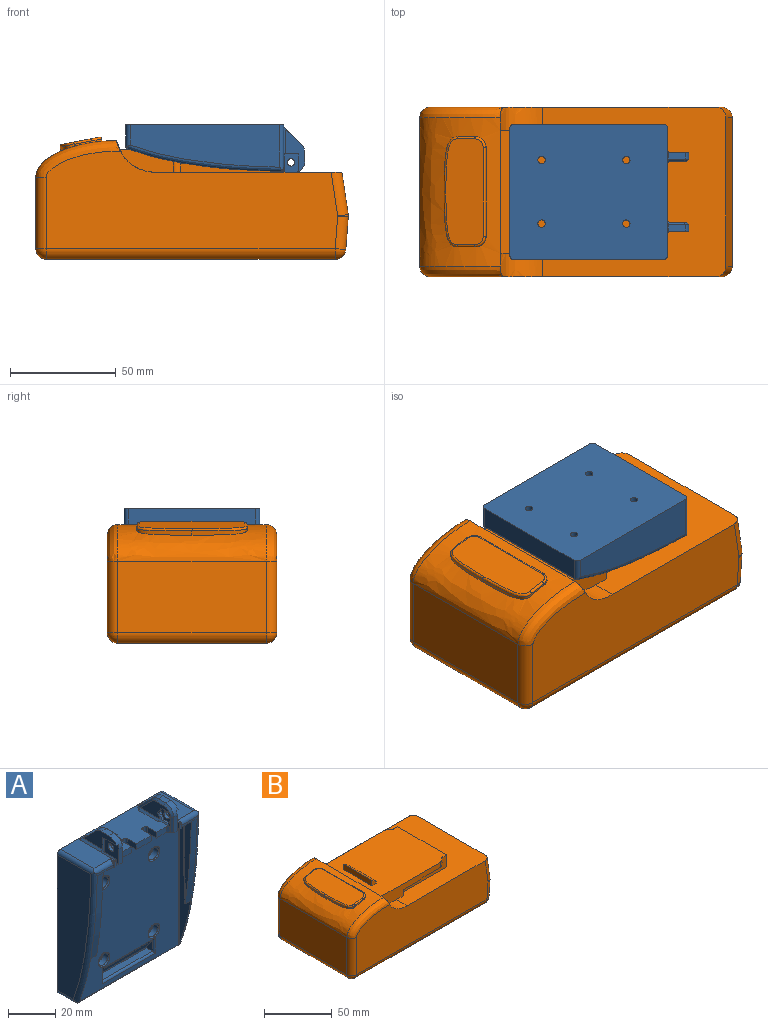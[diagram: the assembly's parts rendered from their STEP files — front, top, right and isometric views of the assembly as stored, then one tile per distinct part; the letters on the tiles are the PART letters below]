
ASSEMBLY  parts=2 mates=1
PART A: 203 faces, bbox 64.2x22.7x84.8 mm
  f0: sphere r=1mm, area 0.3mm2, adj f3,f4,f9,f104
  f1: plane 3.46x1mm, normal (0,0,-1), area 3.5mm2, adj f7,f12,f16,f17
  f2: plane 3x2.62mm, normal (0,0.95,-0.32), area 8.1mm2, adj f4,f21,f105,f106,f107
  f3: cylinder r=1mm len=2.5mm, axis (1,0,0), area 0.8mm2, adj f0,f4,f10,f21
  f4: plane 13.43x3.2mm, normal (0,1,0), area 39.7mm2, adj f0,f2,f3,f21,f104
  f5: plane 25.37x2.5mm, normal (0,1,0), area 63.4mm2, adj f6,f8,f21,f22,f107
  f6: cylinder r=0.5mm len=5.3mm, axis (0,1,0), area 4.2mm2, adj f5,f21,f22,f23
  f7: plane 3x1.73mm, normal (0,-0.87,-0.5), area 3.5mm2, adj f1,f12,f28,f29
  f8: cylinder r=1mm len=27.87mm, axis (0,0,-1), area 41.8mm2, adj f5,f24,f32,f106
  f9: cylinder r=1mm len=1mm, axis (0,-1,0), area 0.2mm2, adj f0,f10,f32,f33,f104
  f10: plane 2.5x0.06mm, normal (0,0,-1), area 0.1mm2, adj f3,f9,f21,f33
  f11: cylinder r=5mm len=3.54mm, axis (1,0,0), area 11.8mm2, adj f13,f15,f31,f37
  f12: plane 6.93x6mm, normal (1,0,0), area 21.6mm2, adj f1,f7,f17,f18,f27,f28,f38
  f13: plane 4.43x3mm, normal (0,0,1), area 13.3mm2, adj f11,f14,f37,f40
  f14: plane 4.43x1mm, normal (0.71,0,0.71), area 6.3mm2, adj f13,f15,f41,f42
  f15: cone r=4mm half-angle=45deg, axis (-1,0,0), area 5mm2, adj f11,f14,f30,f42
  f16: plane 4.04x0.5mm, normal (0.71,0,-0.71), area 2.7mm2, adj f1,f29,f42,f43
  f17: plane 3x1.73mm, normal (0,0.87,-0.5), area 3.5mm2, adj f1,f12,f18,f43
  f18: plane 3x1.73mm, normal (0,0.87,0.5), area 3.5mm2, adj f12,f17,f27,f44
  f19: plane 6x6mm, normal (0,-1,0), area 12.4mm2, adj f26,f47
  f20: plane 6x6mm, normal (0,-1,0), area 12.4mm2, adj f25,f48
  f21: plane 66.43x7.22mm, normal (1,0,0), area 322.6mm2, adj f2,f3,f4,f5,f6,f10,f45,f50
  f22: plane 5.3x2mm, normal (0,0,-1), area 10.6mm2, adj f5,f6,f24,f51
  f23: sphere r=0.5mm, area 0.5mm2, adj f6,f50,f51
  f24: cylinder r=1mm len=6.3mm, axis (0,-1,0), area 9.1mm2, adj f8,f22,f32,f52
  f25: cylinder r=3mm len=6mm, axis (0,-1,0), area 56.5mm2, adj f20,f54
  f26: cylinder r=3mm len=6mm, axis (0,-1,0), area 56.5mm2, adj f19,f55
  f27: plane 3.46x1mm, normal (0,0,1), area 3.5mm2, adj f12,f18,f28,f56
  f28: plane 3x1.73mm, normal (0,-0.87,0.5), area 3.5mm2, adj f7,f12,f27,f57
  f29: plane 3.5x2.31mm, normal (0.71,-0.61,-0.35), area 2.7mm2, adj f7,f16,f42,f57
  f30: plane 8.95x8.24mm, normal (0.71,0.5,0.5), area 15.1mm2, adj f15,f31,f42,f59
  f31: plane 8.24x8.24mm, normal (0,0.71,0.71), area 35.3mm2, adj f11,f30,f37,f60,f61
  f32: plane 44.58x10.5mm, normal (1,0,0), area 131.8mm2, adj f8,f9,f24,f33,f53,f65,f104,f105
  f33: extruded ~45x4mm, area 157.9mm2, adj f9,f10,f32,f45,f65,f66
  f34: plane 1.5x0.68mm, normal (-1,0,0), area 0.3mm2, adj f63,f64,f67
  f35: sphere r=0.5mm, area 0.4mm2, adj f62,f63,f67
  f36: cylinder r=0.5mm len=1mm, axis (-0.71,0,-0.71), area 0.4mm2, adj f61,f62,f68,f69
  f37: plane 19.99x9mm, normal (-1,0,0), area 84.5mm2, adj f11,f13,f31,f39,f40,f61,f70
  f38: cylinder r=1.75mm len=3.5mm, axis (-1,0,0), area 16.5mm2, adj f12,f71
  f39: plane 8.19x1mm, normal (0,0,-1), area 8.2mm2, adj f37,f40,f70,f71
  f40: cylinder r=5mm len=5mm, axis (-1,0,0), area 21.3mm2, adj f13,f37,f39,f41,f71,f72
  f41: cone r=4mm half-angle=45deg, axis (-1,0,0), area 10mm2, adj f14,f40,f42,f73
  f42: plane 18.09x8mm, normal (1,0,0), area 70.1mm2, adj f14,f15,f16,f29,f30,f41,f43,f57
  f43: plane 3.5x2.15mm, normal (0.71,0.61,-0.35), area 2.6mm2, adj f16,f17,f42,f44,f73
  f44: plane 3.5x2.15mm, normal (0.71,0.61,0.35), area 2.6mm2, adj f18,f43,f56,f73,f74
  f45: bspline ~73.6x12.79mm, area 230.3mm2, adj f21,f33,f46,f49,f50,f64,f66,f82
  f46: bspline ~2.41x2mm, area 0.9mm2, adj f45,f49,f84
  f47: torus R=2.25mm, axis (0,-1,0), area 9.5mm2, adj f19,f85
  f48: torus R=2.25mm, axis (0,-1,0), area 9.5mm2, adj f20,f86
  f49: bspline ~0.88x0.76mm, area 0.1mm2, adj f45,f46,f50,f84,f90
  f50: cylinder r=0.5mm len=66.93mm, axis (0,0,-1), area 52.4mm2, adj f21,f23,f45,f49,f90,f102
  f51: cylinder r=0.5mm len=2mm, axis (1,0,0), area 1.6mm2, adj f22,f23,f52,f102
  f52: torus R=1.5mm, axis (0,1,0), area 1.5mm2, adj f24,f51,f53,f102
  f53: cylinder r=0.5mm len=2.07mm, axis (0,0,-1), area 1.6mm2, adj f32,f52,f89,f102
  f54: torus R=3.5mm, axis (0,1,0), area 15.7mm2, adj f25,f102
  f55: torus R=3.5mm, axis (0,1,0), area 15.7mm2, adj f26,f102
  f56: plane 4.04x0.5mm, normal (0.71,0,0.71), area 2.7mm2, adj f27,f44,f57,f100
  f57: plane 3.5x2.31mm, normal (0.71,-0.61,0.35), area 3.5mm2, adj f28,f29,f42,f56,f58,f100
  f58: plane 11.74x1mm, normal (0.71,0,0.71), area 16.2mm2, adj f42,f57,f59,f100
  f59: bspline ~2.83x2mm, area 2.6mm2, adj f30,f58,f60,f100
  f60: plane 4x0.71mm, normal (0,0.38,0.92), area 2.9mm2, adj f31,f59,f61,f100
  f61: plane 21.41x1mm, normal (-0.71,0,0.71), area 23.3mm2, adj f31,f36,f37,f60,f69,f70,f100
  f62: cylinder r=0.5mm len=0.71mm, axis (1,0,0), area 0.5mm2, adj f35,f36,f68,f100
  f63: cylinder r=0.5mm len=2mm, axis (0,1,0), area 1.1mm2, adj f34,f35,f64,f100
  f64: cylinder r=2mm len=11.44mm, axis (-1,0,0), area 32.7mm2, adj f34,f45,f63,f66,f82,f100
  f65: cylinder r=0.5mm len=10.5mm, axis (0,1,0), area 8.2mm2, adj f32,f33,f89,f96
  f66: plane 9.92x1.14mm, normal (0,-1,0), area 9.7mm2, adj f33,f45,f64,f67,f96
  f67: cylinder r=0.5mm len=2.5mm, axis (0,0,1), area 2mm2, adj f34,f35,f66,f68,f96
  f68: plane 2.79x1mm, normal (0,-1,0), area 2.5mm2, adj f36,f62,f67,f69,f96
  f69: plane 8.91x3.71mm, normal (1,0,0), area 30.4mm2, adj f36,f61,f68,f70,f96
  f70: plane 10.2x1.5mm, normal (0,-1,0), area 12.1mm2, adj f37,f39,f61,f69,f71,f96
  f71: plane 10.2x8.7mm, normal (-1,0,0), area 78.8mm2, adj f38,f39,f40,f70,f72,f96
  f72: plane 8x2mm, normal (0,-1,0), area 16mm2, adj f40,f71,f73,f96
  f73: plane 8x1mm, normal (0.71,-0.71,0), area 11.2mm2, adj f41,f42,f43,f44,f72,f74,f96
  f74: plane 6x1.73mm, normal (1,0,0), area 4.1mm2, adj f44,f73,f75,f96,f100
  f75: plane 3x1mm, normal (0.71,-0.71,0), area 4.2mm2, adj f74,f76,f96,f100
  f76: plane 6x3mm, normal (0,-1,0), area 18mm2, adj f75,f77,f96,f100
  f77: plane 5.5x3mm, normal (1,0,0), area 16.5mm2, adj f76,f78,f96,f100
  f78: cylinder r=1mm len=3mm, axis (0,0,-1), area 4.7mm2, adj f77,f79,f96,f100
  f79: plane 3x1mm, normal (0,-1,0), area 3mm2, adj f78,f80,f96,f100
  f80: cylinder r=1mm len=3mm, axis (0,0,-1), area 4.7mm2, adj f79,f81,f96,f100
  f81: plane 5.5x3mm, normal (-1,0,0), area 16.5mm2, adj f80,f96,f100,f101
  f82: cylinder r=2mm len=21.44mm, axis (0,-1,0), area 65.1mm2, adj f45,f64,f83,f98,f100
  f83: plane 70.51x20.02mm, normal (-1,0,0), area 1180.4mm2, adj f45,f82,f84,f98
  f84: cylinder r=2mm len=10.66mm, axis (0,-1,0), area 32.3mm2, adj f46,f49,f83,f98,f99
  f85: cylinder r=1.75mm len=7mm, axis (0,-1,0), area 77mm2, adj f47,f98
  f86: cylinder r=1.75mm len=7mm, axis (0,-1,0), area 77mm2, adj f48,f98
  f87: plane 5.66x3.46mm, normal (1,0,0), area 10.9mm2, adj f88,f91,f93,f103
  f88: cylinder r=1mm len=7.97mm, axis (0,0,-1), area 10.6mm2, adj f87,f92,f93,f94,f102
  f89: sphere r=0.5mm, area 0.5mm2, adj f53,f65,f95
  f90: torus R=1mm, axis (0,0,-1), area 0.3mm2, adj f49,f50,f97,f99
  f91: plane 30x0.66mm, normal (0,-1,0), area 19.7mm2, adj f87,f93,f103,f195
  f92: cylinder r=1mm len=32mm, axis (-1,0,0), area 41.1mm2, adj f88,f93,f102,f196
  f93: plane 30.06x5.35mm, normal (0,-0.82,-0.57), area 195mm2, adj f87,f88,f91,f92,f195,f196
  f94: cylinder r=1mm len=32mm, axis (1,0,0), area 48.7mm2, adj f88,f102,f103,f196
  f95: cylinder r=0.5mm len=52mm, axis (-1,0,0), area 40.8mm2, adj f89,f96,f102,f197
  f96: plane 52x11mm, normal (0,0,-1), area 429.7mm2, adj f65,f66,f67,f68,f69,f70,f71,f72
  f97: cylinder r=0.5mm len=59mm, axis (-1,0,0), area 46.3mm2, adj f90,f99,f102,f198
  f98: plane 74.5x64mm, normal (0,1,0), area 4726.1mm2, adj f82,f83,f84,f85,f86,f99,f100,f190
  f99: plane 60x10.63mm, normal (0,0,-1), area 630mm2, adj f84,f90,f97,f98,f192,f198
  f100: plane 60x22mm, normal (0,0,1), area 947.2mm2, adj f56,f57,f58,f59,f60,f61,f62,f63
  f101: plane 9x3mm, normal (0,-1,0), area 27mm2, adj f81,f96,f100,f189
  f102: plane 70.5x59mm, normal (0,-1,0), area 3726.5mm2, adj f50,f51,f52,f53,f54,f55,f88,f92
  f103: plane 30x3.46mm, normal (0,0,1), area 103.8mm2, adj f87,f91,f94,f195
  f104: cylinder r=0.5mm len=13.17mm, axis (0,0,-1), area 10mm2, adj f0,f4,f9,f32,f105
  f105: cylinder r=0.5mm len=1.36mm, axis (0,0.32,0.95), area 1mm2, adj f2,f32,f104,f106
  f106: bspline ~1.66x1mm, area 0.9mm2, adj f2,f8,f105,f107
  f107: cylinder r=0.5mm len=2.5mm, axis (-1,0,0), area 0.4mm2, adj f2,f5,f21,f106
  f108: sphere r=1mm, area 0.3mm2, adj f111,f112,f117,f199
  f109: plane 3.46x1mm, normal (0,0,-1), area 3.5mm2, adj f115,f120,f124,f125
  f110: plane 3x2.62mm, normal (0,0.95,-0.32), area 8.1mm2, adj f112,f129,f200,f201,f202
  f111: cylinder r=1mm len=2.5mm, axis (-1,0,0), area 0.8mm2, adj f108,f112,f118,f129
  f112: plane 13.43x3.2mm, normal (0,1,0), area 39.7mm2, adj f108,f110,f111,f129,f199
  f113: plane 25.37x2.5mm, normal (0,1,0), area 63.4mm2, adj f114,f116,f129,f130,f202
  f114: cylinder r=0.5mm len=5.3mm, axis (0,1,0), area 4.2mm2, adj f113,f129,f130,f131
  f115: plane 3x1.73mm, normal (0,-0.87,-0.5), area 3.5mm2, adj f109,f120,f136,f137
  f116: cylinder r=1mm len=27.87mm, axis (0,0,-1), area 41.8mm2, adj f113,f132,f140,f201
  f117: cylinder r=1mm len=1mm, axis (0,-1,0), area 0.2mm2, adj f108,f118,f140,f141,f199
  f118: plane 2.5x0.06mm, normal (0,0,-1), area 0.1mm2, adj f111,f117,f129,f141
  f119: cylinder r=5mm len=3.54mm, axis (-1,0,0), area 11.8mm2, adj f121,f123,f139,f145
  f120: plane 6.93x6mm, normal (-1,0,0), area 21.6mm2, adj f109,f115,f125,f126,f135,f136,f146
  f121: plane 4.43x3mm, normal (0,0,1), area 13.3mm2, adj f119,f122,f145,f148
  f122: plane 4.43x1mm, normal (-0.71,0,0.71), area 6.3mm2, adj f121,f123,f149,f150
  f123: cone r=4mm half-angle=45deg, axis (1,0,0), area 5mm2, adj f119,f122,f138,f150
  f124: plane 4.04x0.5mm, normal (-0.71,0,-0.71), area 2.7mm2, adj f109,f137,f150,f151
  f125: plane 3x1.73mm, normal (0,0.87,-0.5), area 3.5mm2, adj f109,f120,f126,f151
  f126: plane 3x1.73mm, normal (0,0.87,0.5), area 3.5mm2, adj f120,f125,f135,f152
  f127: plane 6x6mm, normal (0,-1,0), area 12.4mm2, adj f134,f155
  f128: plane 6x6mm, normal (0,-1,0), area 12.4mm2, adj f133,f156
  f129: plane 66.43x7.22mm, normal (-1,0,0), area 322.6mm2, adj f110,f111,f112,f113,f114,f118,f153,f158
  f130: plane 5.3x2mm, normal (0,0,-1), area 10.6mm2, adj f113,f114,f132,f159
  f131: sphere r=0.5mm, area 0.4mm2, adj f114,f158,f159
  f132: cylinder r=1mm len=6.3mm, axis (0,-1,0), area 9.1mm2, adj f116,f130,f140,f160
  f133: cylinder r=3mm len=6mm, axis (0,-1,0), area 56.5mm2, adj f128,f162
  f134: cylinder r=3mm len=6mm, axis (0,-1,0), area 56.5mm2, adj f127,f163
  f135: plane 3.46x1mm, normal (0,0,1), area 3.5mm2, adj f120,f126,f136,f164
  f136: plane 3x1.73mm, normal (0,-0.87,0.5), area 3.5mm2, adj f115,f120,f135,f165
  f137: plane 3.5x2.31mm, normal (-0.71,-0.61,-0.35), area 2.7mm2, adj f115,f124,f150,f165
  f138: plane 8.95x8.24mm, normal (-0.71,0.5,0.5), area 15.1mm2, adj f123,f139,f150,f167
  f139: plane 8.24x8.24mm, normal (0,0.71,0.71), area 35.3mm2, adj f119,f138,f145,f168,f169
  f140: plane 44.58x10.5mm, normal (-1,0,0), area 131.8mm2, adj f116,f117,f132,f141,f161,f173,f199,f200
  f141: extruded ~45x4mm, area 157.9mm2, adj f117,f118,f140,f153,f173,f174
  f142: plane 1.5x0.68mm, normal (1,0,0), area 0.3mm2, adj f171,f172,f175
  f143: sphere r=0.5mm, area 0.5mm2, adj f170,f171,f175
  f144: cylinder r=0.5mm len=1mm, axis (0.71,0,-0.71), area 0.4mm2, adj f169,f170,f176,f177
  f145: plane 19.99x9mm, normal (1,0,0), area 84.5mm2, adj f119,f121,f139,f147,f148,f169,f178
  f146: cylinder r=1.75mm len=3.5mm, axis (1,0,0), area 16.5mm2, adj f120,f179
  f147: plane 8.19x1mm, normal (0,0,-1), area 8.2mm2, adj f145,f148,f178,f179
  f148: cylinder r=5mm len=5mm, axis (1,0,0), area 21.3mm2, adj f121,f145,f147,f149,f179,f180
  f149: cone r=4mm half-angle=45deg, axis (1,0,0), area 10mm2, adj f122,f148,f150,f181
  f150: plane 18.09x8mm, normal (-1,0,0), area 70.1mm2, adj f122,f123,f124,f137,f138,f149,f151,f165
  f151: plane 3.5x2.15mm, normal (-0.71,0.61,-0.35), area 2.6mm2, adj f124,f125,f150,f152,f181
  f152: plane 3.5x2.15mm, normal (-0.71,0.61,0.35), area 2.6mm2, adj f126,f151,f164,f181,f182
  f153: bspline ~73.6x12.79mm, area 230.3mm2, adj f129,f141,f154,f157,f158,f172,f174,f190
  f154: bspline ~2.41x2mm, area 0.9mm2, adj f153,f157,f192
  f155: torus R=2.25mm, axis (0,-1,0), area 9.5mm2, adj f127,f193
  f156: torus R=2.25mm, axis (0,-1,0), area 9.5mm2, adj f128,f194
  f157: bspline ~0.88x0.76mm, area 0.1mm2, adj f153,f154,f158,f192,f198
  f158: cylinder r=0.5mm len=66.93mm, axis (0,0,-1), area 52.4mm2, adj f102,f129,f131,f153,f157,f198
  f159: cylinder r=0.5mm len=2mm, axis (-1,0,0), area 1.6mm2, adj f102,f130,f131,f160
  f160: torus R=1.5mm, axis (0,1,0), area 1.5mm2, adj f102,f132,f159,f161
  f161: cylinder r=0.5mm len=2.07mm, axis (0,0,-1), area 1.6mm2, adj f102,f140,f160,f197
  f162: torus R=3.5mm, axis (0,1,0), area 15.7mm2, adj f102,f133
  f163: torus R=3.5mm, axis (0,1,0), area 15.7mm2, adj f102,f134
  f164: plane 4.04x0.5mm, normal (-0.71,0,0.71), area 2.7mm2, adj f100,f135,f152,f165
  f165: plane 3.5x2.31mm, normal (-0.71,-0.61,0.35), area 3.5mm2, adj f100,f136,f137,f150,f164,f166
  f166: plane 11.74x1mm, normal (-0.71,0,0.71), area 16.2mm2, adj f100,f150,f165,f167
  f167: bspline ~2.83x2mm, area 2.6mm2, adj f100,f138,f166,f168
  f168: plane 4x0.71mm, normal (0,0.38,0.92), area 2.9mm2, adj f100,f139,f167,f169
  f169: plane 21.41x1mm, normal (0.71,0,0.71), area 23.3mm2, adj f100,f139,f144,f145,f168,f177,f178
  f170: cylinder r=0.5mm len=0.71mm, axis (-1,0,0), area 0.5mm2, adj f100,f143,f144,f176
  f171: cylinder r=0.5mm len=2mm, axis (0,1,0), area 1.1mm2, adj f100,f142,f143,f172
  f172: cylinder r=2mm len=11.44mm, axis (1,0,0), area 32.7mm2, adj f100,f142,f153,f171,f174,f190
  f173: cylinder r=0.5mm len=10.5mm, axis (0,1,0), area 8.2mm2, adj f96,f140,f141,f197
  f174: plane 9.92x1.14mm, normal (0,-1,0), area 9.7mm2, adj f96,f141,f153,f172,f175
  f175: cylinder r=0.5mm len=2.5mm, axis (0,0,1), area 2mm2, adj f96,f142,f143,f174,f176
  f176: plane 2.79x1mm, normal (0,-1,0), area 2.5mm2, adj f96,f144,f170,f175,f177
  f177: plane 8.91x3.71mm, normal (-1,0,0), area 30.4mm2, adj f96,f144,f169,f176,f178
  f178: plane 10.2x1.5mm, normal (0,-1,0), area 12.1mm2, adj f96,f145,f147,f169,f177,f179
  f179: plane 10.2x8.7mm, normal (1,0,0), area 78.8mm2, adj f96,f146,f147,f148,f178,f180
  f180: plane 8x2mm, normal (0,-1,0), area 16mm2, adj f96,f148,f179,f181
  f181: plane 8x1mm, normal (-0.71,-0.71,0), area 11.2mm2, adj f96,f149,f150,f151,f152,f180,f182
  f182: plane 6x1.73mm, normal (-1,0,0), area 4.1mm2, adj f96,f100,f152,f181,f183
  f183: plane 3x1mm, normal (-0.71,-0.71,0), area 4.2mm2, adj f96,f100,f182,f184
  f184: plane 6x3mm, normal (0,-1,0), area 18mm2, adj f96,f100,f183,f185
  f185: plane 5.5x3mm, normal (-1,0,0), area 16.5mm2, adj f96,f100,f184,f186
  f186: cylinder r=1mm len=3mm, axis (0,0,-1), area 4.7mm2, adj f96,f100,f185,f187
  f187: plane 3x1mm, normal (0,-1,0), area 3mm2, adj f96,f100,f186,f188
  f188: cylinder r=1mm len=3mm, axis (0,0,-1), area 4.7mm2, adj f96,f100,f187,f189
  f189: plane 5.5x3mm, normal (1,0,0), area 16.5mm2, adj f96,f100,f101,f188
  f190: cylinder r=2mm len=21.44mm, axis (0,-1,0), area 65.1mm2, adj f98,f100,f153,f172,f191
  f191: plane 70.51x20.02mm, normal (1,0,0), area 1180.4mm2, adj f98,f153,f190,f192
  f192: cylinder r=2mm len=10.66mm, axis (0,-1,0), area 32.3mm2, adj f98,f99,f154,f157,f191
  f193: cylinder r=1.75mm len=7mm, axis (0,-1,0), area 77mm2, adj f98,f155
  f194: cylinder r=1.75mm len=7mm, axis (0,-1,0), area 77mm2, adj f98,f156
  f195: plane 5.66x3.46mm, normal (-1,0,0), area 10.9mm2, adj f91,f93,f103,f196
  f196: cylinder r=1mm len=7.97mm, axis (0,0,-1), area 10.6mm2, adj f92,f93,f94,f102,f195
  f197: sphere r=0.5mm, area 0.4mm2, adj f95,f161,f173
  f198: torus R=1mm, axis (0,0,-1), area 0.3mm2, adj f97,f99,f157,f158
  f199: cylinder r=0.5mm len=13.17mm, axis (0,0,-1), area 10mm2, adj f108,f112,f117,f140,f200
  f200: cylinder r=0.5mm len=1.36mm, axis (0,0.32,0.95), area 1mm2, adj f110,f140,f199,f201
  f201: bspline ~1.66x1mm, area 0.9mm2, adj f110,f116,f200,f202
  f202: cylinder r=0.5mm len=2.5mm, axis (1,0,0), area 0.4mm2, adj f110,f113,f129,f201
PART B: 100 faces, bbox 147.8x84.3x58 mm
  f0: plane 51x11mm, normal (1,0,0), area 350.6mm2, adj f5,f9,f10,f45,f46,f47,f48,f49
  f1: plane 70x33.75mm, normal (-1,0,0), area 2362.5mm2, adj f28,f30,f31,f77
  f2: plane 16.74x3.5mm, normal (0,0,-1), area 56mm2, adj f3,f5,f12,f13
  f3: plane 64.46x12mm, normal (0,-1,0), area 421.6mm2, adj f2,f9,f10,f11,f12,f13,f14,f25
  f4: plane 4.6x1.53mm, normal (0.7,-0.71,0), area 9.9mm2, adj f10,f11,f14,f15
  f5: plane 45x11mm, normal (0,-1,0), area 291.3mm2, adj f0,f2,f9,f10,f11,f12,f13,f15
  f6: plane 137.5x47.17mm, normal (0,-1,0), area 5208.3mm2, adj f9,f22,f23,f24,f25,f29,f31,f33
  f7: plane 136.36x70mm, normal (0,0,-1), area 9545.3mm2, adj f30,f33,f35,f79
  f8: plane 70x1mm, normal (1,0,0), area 70mm2, adj f20,f21,f23,f72
  f9: plane 86.87x80.32mm, normal (0,0,1), area 4964.3mm2, adj f0,f3,f5,f6,f13,f20,f22,f25
  f10: plane 75.5x58mm, normal (0,0,1), area 4186.5mm2, adj f0,f3,f4,f5,f14,f15,f16,f17
  f11: plane 25.49x3.5mm, normal (0,0,-1), area 77.9mm2, adj f3,f4,f5,f12,f14,f15
  f12: plane 3.5x2.7mm, normal (0.32,0,-0.95), area 10mm2, adj f2,f3,f5,f11
  f13: cylinder r=3.5mm len=5.5mm, axis (0,0,-1), area 30.2mm2, adj f2,f3,f5,f9
  f14: cylinder r=3.5mm len=4.6mm, axis (0,0,-1), area 12.5mm2, adj f3,f4,f10,f11
  f15: cylinder r=3.5mm len=4.6mm, axis (0,0,-1), area 12.5mm2, adj f4,f5,f10,f11
  f16: plane 29x4.96mm, normal (-1,0,0), area 143.9mm2, adj f10,f17,f19,f70
  f17: plane 5x4.96mm, normal (0,-1,0), area 16.2mm2, adj f10,f16,f18,f19
  f18: plane 29x1.5mm, normal (1,0,0), area 43.5mm2, adj f10,f17,f19,f70
  f19: plane 29x5mm, normal (0.57,0,0.82), area 176.4mm2, adj f16,f17,f18,f70
  f20: plane 70x20mm, normal (0.99,0,0.15), area 1415.7mm2, adj f8,f9,f22,f71
  f21: plane 70x15.37mm, normal (1,0,-0.07), area 1079.2mm2, adj f8,f24,f35,f73
  f22: cylinder r=5mm len=21.48mm, axis (0.15,0,-0.99), area 160.3mm2, adj f6,f9,f20,f23
  f23: cylinder r=5mm len=5mm, axis (0,0,-1), area 5.7mm2, adj f6,f8,f22,f24
  f24: cylinder r=5mm len=15.75mm, axis (0.07,0,1), area 120.4mm2, adj f6,f21,f23,f34
  f25: bspline ~44x19.95mm, area 284.8mm2, adj f3,f6,f9,f26,f28,f29
  f26: plane 4.11x1.58mm, normal (0,1,0), area 2.7mm2, adj f10,f25,f27
  f27: plane 58x4mm, normal (1,0,0), area 232mm2, adj f10,f26,f28,f75
  f28: extruded ~70x38mm, area 2154.2mm2, adj f1,f25,f27,f29,f36,f37,f38,f39
  f29: bspline ~42.62x24.87mm, area 336.8mm2, adj f6,f25,f28,f31
  f30: cylinder r=5mm len=70mm, axis (0,-1,0), area 549.8mm2, adj f1,f7,f32,f78
  f31: cylinder r=5mm len=33.75mm, axis (0,0,1), area 265.1mm2, adj f1,f6,f29,f32
  f32: sphere r=5mm, area 39.3mm2, adj f30,f31,f33
  f33: cylinder r=5mm len=136.36mm, axis (1,0,0), area 1071mm2, adj f6,f7,f32,f34
  f34: sphere r=5mm, area 37.4mm2, adj f24,f33,f35
  f35: cylinder r=5mm len=70mm, axis (0,1,0), area 523.6mm2, adj f7,f21,f34,f80
  f36: extruded ~26x7.03mm, area 53mm2, adj f28,f37,f44,f81
  f37: plane 8.29x2.57mm, normal (0,-1,0), area 6.5mm2, adj f28,f36,f38,f43
  f38: cylinder r=5mm len=5.12mm, axis (-0.19,0,0.98), area 7.3mm2, adj f28,f37,f39,f42
  f39: plane 42x1.08mm, normal (0.98,0,0.19), area 46.2mm2, adj f28,f38,f41,f83
  f40: plane 50x17.68mm, normal (-0.19,0,0.98), area 859mm2, adj f41,f42,f43,f44,f84,f85,f86
  f41: cylinder r=1mm len=42mm, axis (0,1,0), area 66mm2, adj f39,f40,f42,f84
  f42: torus R=4mm, axis (-0.19,0,0.98), area 11.4mm2, adj f38,f40,f41,f43
  f43: cylinder r=1mm len=8.28mm, axis (0.98,0,0.19), area 12.9mm2, adj f37,f40,f42,f44
  f44: bspline ~29.5x12.52mm, area 44.8mm2, adj f36,f40,f43,f86
  f45: plane 21x3mm, normal (0,1,0), area 63mm2, adj f0,f9,f58,f59
  f46: plane 21x9mm, normal (0,0,-1), area 189mm2, adj f0,f47,f59,f88
  f47: plane 21x5.5mm, normal (0,-1,0), area 115.5mm2, adj f0,f46,f48,f59
  f48: cylinder r=1mm len=21mm, axis (1,0,0), area 33mm2, adj f0,f47,f49,f59
  f49: plane 21x1mm, normal (0,0,-1), area 21mm2, adj f0,f48,f50,f59
  f50: cylinder r=1mm len=21mm, axis (1,0,0), area 33mm2, adj f0,f49,f51,f59
  f51: plane 21x5.5mm, normal (0,1,0), area 115.5mm2, adj f0,f50,f52,f59
  f52: plane 21x9mm, normal (0,0,-1), area 189mm2, adj f0,f51,f53,f59
  f53: plane 21x5.5mm, normal (0,-1,0), area 115.5mm2, adj f0,f52,f54,f59
  f54: cylinder r=1mm len=21mm, axis (1,0,0), area 33mm2, adj f0,f53,f55,f59
  f55: plane 21x1mm, normal (0,0,-1), area 21mm2, adj f0,f54,f56,f59
  f56: cylinder r=1mm len=21mm, axis (1,0,0), area 33mm2, adj f0,f55,f57,f59
  f57: plane 21x5.5mm, normal (0,1,0), area 115.5mm2, adj f0,f56,f58,f59
  f58: plane 21x2.85mm, normal (0,0,-1), area 59.8mm2, adj f0,f45,f57,f59
  f59: plane 44.7x9.5mm, normal (1,0,0), area 210.4mm2, adj f9,f45,f46,f47,f48,f49,f50,f51
  f60: plane 16.5x3.5mm, normal (0,0,-1), area 55.1mm2, adj f61,f63,f66,f67
  f61: plane 64.46x12mm, normal (0,1,0), area 361.7mm2, adj f9,f10,f60,f65,f66,f67,f68,f74
  f62: plane 3x1.53mm, normal (0.7,0.71,0), area 6.4mm2, adj f10,f65,f68,f69
  f63: plane 45x11mm, normal (0,1,0), area 356.2mm2, adj f0,f9,f10,f60,f65,f66,f67,f69
  f64: plane 137.5x47.17mm, normal (0,1,0), area 5208.3mm2, adj f9,f71,f72,f73,f74,f76,f77,f79
  f65: plane 25.43x3.5mm, normal (0,0,-1), area 77.8mm2, adj f61,f62,f63,f66,f68,f69
  f66: plane 3.5x3mm, normal (0.32,0,-0.95), area 11.1mm2, adj f60,f61,f63,f65
  f67: cylinder r=3.5mm len=7mm, axis (0,0,-1), area 38.5mm2, adj f9,f60,f61,f63
  f68: cylinder r=3.5mm len=3mm, axis (0,0,-1), area 8.1mm2, adj f10,f61,f62,f65
  f69: cylinder r=3.5mm len=3mm, axis (0,0,-1), area 8.1mm2, adj f10,f62,f63,f65
  f70: plane 5x4.96mm, normal (0,1,0), area 16.2mm2, adj f10,f16,f18,f19
  f71: cylinder r=5mm len=21.48mm, axis (0.15,0,-0.99), area 160.3mm2, adj f9,f20,f64,f72
  f72: cylinder r=5mm len=5mm, axis (0,0,-1), area 5.7mm2, adj f8,f64,f71,f73
  f73: cylinder r=5mm len=15.75mm, axis (0.07,0,1), area 120.4mm2, adj f21,f64,f72,f80
  f74: bspline ~44x19.95mm, area 284.8mm2, adj f9,f28,f61,f64,f75,f76
  f75: plane 4.11x1.58mm, normal (0,-1,0), area 2.7mm2, adj f10,f27,f74
  f76: bspline ~42.62x24.87mm, area 336.9mm2, adj f28,f64,f74,f77
  f77: cylinder r=5mm len=33.75mm, axis (0,0,1), area 265.1mm2, adj f1,f64,f76,f78
  f78: sphere r=5mm, area 53.5mm2, adj f30,f77,f79
  f79: cylinder r=5mm len=136.36mm, axis (1,0,0), area 1071mm2, adj f7,f64,f78,f80
  f80: sphere r=5mm, area 23.5mm2, adj f35,f73,f79
  f81: extruded ~26x7.03mm, area 53mm2, adj f28,f36,f82,f86
  f82: plane 8.29x2.57mm, normal (0,1,0), area 6.5mm2, adj f28,f81,f83,f85
  f83: cylinder r=5mm len=5.12mm, axis (-0.19,0,0.98), area 7.3mm2, adj f28,f39,f82,f84
  f84: torus R=4mm, axis (-0.19,0,0.98), area 11.4mm2, adj f40,f41,f83,f85
  f85: cylinder r=1mm len=8.28mm, axis (0.98,0,0.19), area 12.9mm2, adj f40,f82,f84,f86
  f86: bspline ~29.5x12.52mm, area 44.8mm2, adj f40,f44,f81,f85
  f87: plane 21x3mm, normal (0,-1,0), area 63mm2, adj f0,f9,f59,f99
  f88: plane 21x5.5mm, normal (0,1,0), area 115.5mm2, adj f0,f46,f59,f89
  f89: cylinder r=1mm len=21mm, axis (1,0,0), area 33mm2, adj f0,f59,f88,f90
  f90: plane 21x1mm, normal (0,0,-1), area 21mm2, adj f0,f59,f89,f91
  f91: cylinder r=1mm len=21mm, axis (1,0,0), area 33mm2, adj f0,f59,f90,f92
  f92: plane 21x5.5mm, normal (0,-1,0), area 115.5mm2, adj f0,f59,f91,f93
  f93: plane 21x9mm, normal (0,0,-1), area 189mm2, adj f0,f59,f92,f94
  f94: plane 21x5.5mm, normal (0,1,0), area 115.5mm2, adj f0,f59,f93,f95
  f95: cylinder r=1mm len=21mm, axis (1,0,0), area 33mm2, adj f0,f59,f94,f96
  f96: plane 21x1mm, normal (0,0,-1), area 21mm2, adj f0,f59,f95,f97
  f97: cylinder r=1mm len=21mm, axis (1,0,0), area 33mm2, adj f0,f59,f96,f98
  f98: plane 21x5.5mm, normal (0,-1,0), area 115.5mm2, adj f0,f59,f97,f99
  f99: plane 21x2.85mm, normal (0,0,-1), area 59.8mm2, adj f0,f59,f87,f98
PLACE A rot(axis=(0.58,0.58,0.58),120deg) t=(37.05,3.47,69.68)mm fixed
PLACE B t=(-3.2,3.47,21.71)mm
MATE fastened B.f16 <-> A.f103  axis (-1,0,0) through (-30.55,3.47,78.67)mm
